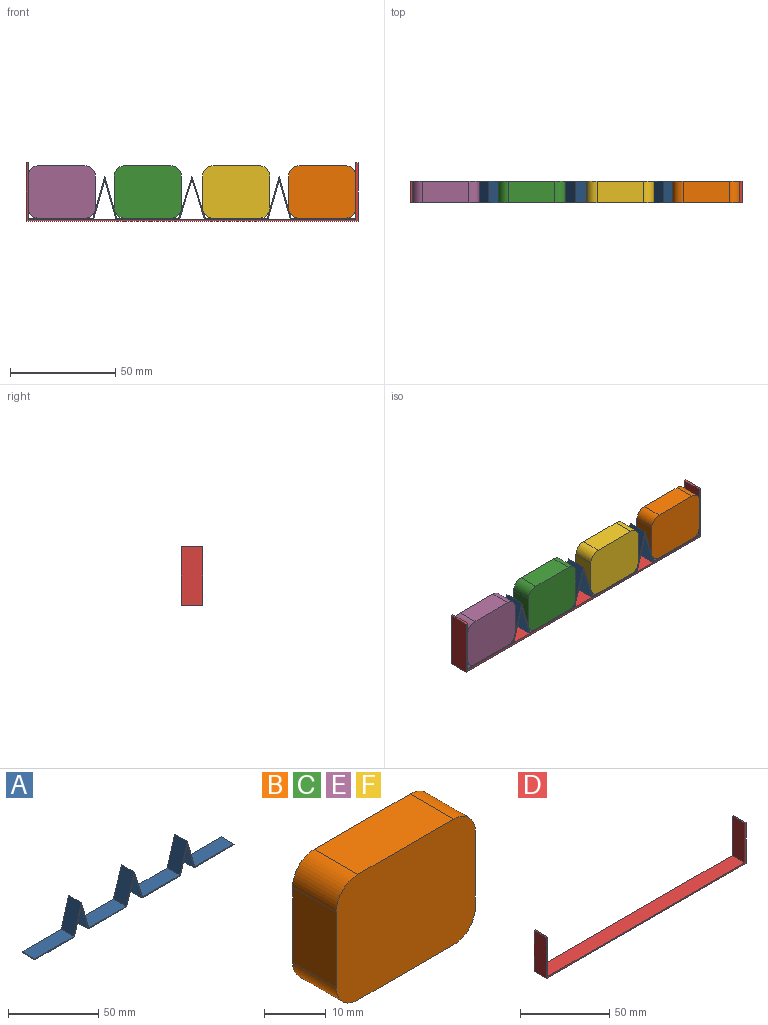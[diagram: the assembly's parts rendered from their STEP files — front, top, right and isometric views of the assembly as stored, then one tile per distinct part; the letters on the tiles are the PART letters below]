
ASSEMBLY  parts=6 mates=12
PART A: 24 faces, bbox 156x10x20.5 mm
  f0: plane 10x0.5mm, normal (1,0,0), area 5mm2, adj f2,f3,f21,f23
  f1: plane 10x0.5mm, normal (-1,0,0), area 5mm2, adj f20,f21,f22,f23
  f2: plane 30.77x10mm, normal (0,0,1), area 307.7mm2, adj f0,f5,f21,f23
  f3: plane 31.15x10mm, normal (0,0,-1), area 311.4mm2, adj f0,f4,f21,f23
  f4: plane 18.69x10mm, normal (-0.96,0,-0.28), area 194.4mm2, adj f3,f7,f21,f23
  f5: plane 20x10mm, normal (0.96,0,0.28), area 208.1mm2, adj f2,f6,f21,f23
  f6: plane 20x10mm, normal (-0.96,0,0.28), area 208mm2, adj f5,f9,f21,f23
  f7: plane 18.69x10mm, normal (0.96,0,-0.28), area 194.4mm2, adj f4,f8,f21,f23
  f8: plane 30.17x10mm, normal (0,0,-1), area 301.7mm2, adj f7,f10,f21,f23
  f9: plane 29.43x10mm, normal (0,0,1), area 294.3mm2, adj f6,f11,f21,f23
  f10: plane 18.85x10mm, normal (-0.95,0,-0.3), area 197.7mm2, adj f8,f13,f21,f23
  f11: plane 20x10mm, normal (0.95,0,0.3), area 209.8mm2, adj f9,f12,f21,f23
  f12: plane 20x10mm, normal (-0.95,0,0.3), area 209.8mm2, adj f11,f15,f21,f23
  f13: plane 18.85x10mm, normal (0.95,0,-0.3), area 197.7mm2, adj f10,f14,f21,f23
  f14: plane 30.17x10mm, normal (0,0,-1), area 301.7mm2, adj f13,f16,f21,f23
  f15: plane 29.43x10mm, normal (0,0,1), area 294.3mm2, adj f12,f17,f21,f23
  f16: plane 18.69x10mm, normal (-0.96,0,-0.28), area 194.4mm2, adj f14,f19,f21,f23
  f17: plane 20x10mm, normal (0.96,0,0.28), area 208mm2, adj f15,f18,f21,f23
  f18: plane 20x10mm, normal (-0.96,0,0.28), area 208.1mm2, adj f17,f21,f22,f23
  f19: plane 18.69x10mm, normal (0.96,0,-0.28), area 194.4mm2, adj f16,f20,f21,f23
  f20: plane 31.15x10mm, normal (0,0,-1), area 311.4mm2, adj f1,f19,f21,f23
  f21: plane 156x20.5mm, normal (0,-1,0), area 121.4mm2, adj f0,f1,f2,f3,f4,f5,f6,f7
  f22: plane 30.77x10mm, normal (0,0,1), area 307.7mm2, adj f1,f18,f21,f23
  f23: plane 156x20.5mm, normal (0,1,0), area 121.4mm2, adj f0,f1,f2,f3,f4,f5,f6,f7
PART B: 10 faces, bbox 32x10x25 mm
  f0: plane 15x10mm, normal (1,0,0), area 150mm2, adj f1,f7,f8,f9
  f1: cylinder r=5mm len=10mm, axis (0,1,0), area 78.5mm2, adj f0,f2,f8,f9
  f2: plane 22x10mm, normal (0,0,1), area 220mm2, adj f1,f3,f8,f9
  f3: cylinder r=5mm len=10mm, axis (0,1,0), area 78.5mm2, adj f2,f4,f8,f9
  f4: plane 15x10mm, normal (-1,0,0), area 150mm2, adj f3,f5,f8,f9
  f5: cylinder r=5mm len=10mm, axis (0,1,0), area 78.5mm2, adj f4,f6,f8,f9
  f6: plane 22x10mm, normal (0,0,-1), area 220mm2, adj f5,f7,f8,f9
  f7: cylinder r=5mm len=10mm, axis (0,1,0), area 78.5mm2, adj f0,f6,f8,f9
  f8: plane 32x25mm, normal (0,-1,0), area 778.5mm2, adj f0,f1,f2,f3,f4,f5,f6,f7
  f9: plane 32x25mm, normal (0,1,0), area 778.5mm2, adj f0,f1,f2,f3,f4,f5,f6,f7
PART C: same geometry as B
PART D: 10 faces, bbox 158x10x28 mm
  f0: plane 10x1mm, normal (0,0,1), area 10mm2, adj f4,f5,f6,f9
  f1: plane 10x1mm, normal (0,0,1), area 10mm2, adj f2,f5,f6,f7
  f2: plane 28x10mm, normal (-1,0,0), area 280mm2, adj f1,f3,f5,f6
  f3: plane 158x10mm, normal (0,0,-1), area 1580mm2, adj f2,f4,f5,f6
  f4: plane 28x10mm, normal (1,0,0), area 280mm2, adj f0,f3,f5,f6
  f5: plane 158x28mm, normal (0,-1,0), area 212mm2, adj f0,f1,f2,f3,f4,f7,f8,f9
  f6: plane 158x28mm, normal (0,1,0), area 212mm2, adj f0,f1,f2,f3,f4,f7,f8,f9
  f7: plane 27x10mm, normal (1,0,0), area 270mm2, adj f1,f5,f6,f8
  f8: plane 156x10mm, normal (0,0,1), area 1560mm2, adj f5,f6,f7,f9
  f9: plane 27x10mm, normal (-1,0,0), area 270mm2, adj f0,f5,f6,f8
PART E: same geometry as B
PART F: same geometry as B
PLACE A t=(82.11,42.78,-57.92)mm fixed
PLACE B t=(163.2,47.78,-17.38)mm
PLACE C t=(80.2,47.78,-17.38)mm
PLACE D t=(19.58,47.78,1.96)mm fixed
PLACE E t=(39.2,47.78,-17.38)mm
PLACE F t=(122.2,47.78,-17.38)mm
MATE planar F.f8 <-> D.f5  axis (0,-1,0) through (119.58,37.78,-12.04)mm
MATE planar A.f21 <-> D.f5  axis (0,-1,0) through (98.58,37.78,-19.95)mm
MATE planar A.f20 <-> D.f8  axis (0,0,-1) through (36.16,47.78,-25.04)mm
MATE planar C.f8 <-> D.f5  axis (0,-1,0) through (77.58,37.78,-12.04)mm
MATE planar B.f8 <-> D.f5  axis (0,-1,0) through (160.58,37.78,-12.04)mm
MATE planar E.f4 <-> D.f7  axis (-1,0,0) through (20.58,42.78,-12.04)mm
MATE planar D.f7 <-> A.f1  axis (1,0,0) through (20.58,47.78,-11.54)mm
MATE planar E.f8 <-> D.f5  axis (0,-1,0) through (36.58,37.78,-12.04)mm
MATE planar E.f6 <-> A.f22  axis (0,0,-1) through (36.58,42.78,-24.54)mm
MATE planar A.f9 <-> F.f6  axis (0,0,1) through (119.64,42.78,-24.54)mm
MATE planar C.f6 <-> A.f15  axis (0,0,-1) through (77.58,42.78,-24.54)mm
MATE planar A.f2 <-> B.f6  axis (0,0,1) through (176.58,42.78,-24.54)mm
